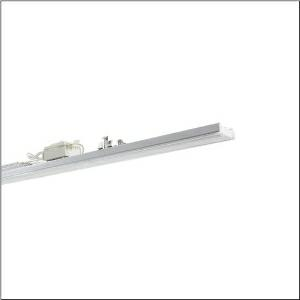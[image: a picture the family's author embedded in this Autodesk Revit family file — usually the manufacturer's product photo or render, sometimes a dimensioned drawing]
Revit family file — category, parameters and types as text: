
# Revit family: licross_r__21_recessed_mo_52tl1ecn48xg_a19d
name_source: partatom
category: Lighting Fixtures
units: mm (PartAtom-declared; Revit-internal decimal feet)

## family parameters
Cut with Voids When Loaded = No
Host = Face
Light Source = No
Part Type = Normal
Room Calculation Point = No
Round Connector Dimension = Use Diameter
Shared = No

## types (1)
- --- (1 x LED, 8020 lm, 44.4 W, 4000K)
    Apparent Load = 44 VA
    CIE Flux Codes = 85 95 99 100 100
    Color Rendering = 80
    Color Temperature = 4000K
    Default Elevation = 1800 mm
    Description = Licross® 21 Recessed MO, luminaire insert, of sheet steel, galvanised, coil coated, white, length: 1.500mm, width: 66mm, height: 67mm, LED rated luminous flux: 8.030lm, light colour: 840, control gear: ON/OFF Multilumen, CLOi, control gear: ECG Multilumen, with plug, 3-pole, with phase selection, mains connection: 220..240V, AC, 50/60Hz, start of lifetime: 44W, end of service life: 53W, internal wiring halogen-free, primary light control with lens, of plastic, primary optical cover: cover, of PMMA, light emission: direct distribution, primary light characteristic: symmetric, protection rating (complete): IP40, insulation class (complete): insulation class I (protective earthing), certification: CE, ENEC, VDE, UKCA, protection symbol: D if used in an environment without relevant dust loads with corresponding accessories, impact resistance: IK06, permissible ambient temperature for indoor applications: -35..+45°C, corresponds to IFS (International Featured Standards) requirements for safety and quality in the food industry, reducing of maximum allowable ambient temperature of 5°C with ceiling mounting, LABS conformity tested according to VDMA 24364:2018-05, packaging unit: 1 piece
    Height = 58 mm
    Lamp = 1 x LED
    Lamp Light Flux = 8020 lm
    Lamp Power = 44.4 W
    Lamp count = 1
    Length = 1500 mm
    Luminous efficacy = 181 lm/W
    Manufacturer = Siteco
    ModVariant = No
    Model = 52TL1ECN48XG
    Mounting Place = Ceiling
    Mounting Type = Pendant
    Number of Poles = 1
    OnlyDefault = Yes
    Power Factor = 1
    Product Name = Licross® 21 Recessed MO
    Product group = luminaire insert | ceiling pendant
    ProductGroupID = 902
    Protection Class = Protection class I
    Protection Degree = IP 40
    RLX_Detail_Level = 1
    RLX_Emergency_Light_Flux = 0 lm
    RLX_Emergency_Type = 0
    RLX_Emergency_Type_DB = No
    RlxData = <blob elided: 22389 chars, md5=377db8e5>
    Socket = socket
    Standby Power = 0 W
    System Light Flux = 8020 lm
    System Power = 44 W
    Type Comments = factory setting: luminous flux: 100 % | (A | C | E) | 103 mA
    Type Image = l_1296930.jpg
    URL = http://relux.com
    VarID = @adj_131387
    Voltage = 0 V
    Weight = 0.00 kg
    Width = 66 mm

## geometry (parser evidence)
native form markers: Blend x4, Sweep x11
no freeform markers — native parametric forms only
